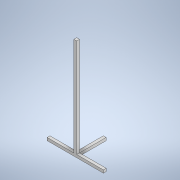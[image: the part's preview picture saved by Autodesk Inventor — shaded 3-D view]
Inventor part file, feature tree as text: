
AUTODESK INVENTOR PART (.ipt)
format: ipt  version: 2020 (Build 240168000, 168)  size: 119,808 bytes
history: native  units: mm
features: extrude x3, sketch x3, projected_geometry x1
ambient origin geometry x8: Origin, YZ Plane, XZ Plane, XY Plane, X Axis, Y Axis, Z Axis, Center Point
bodies: Solid1 (feature_tree)
feature tree (7):
  extrude  "Extrusion1"  Depth=20.0mm
  extrude  "Extrusion2"  Depth=400.0mm
  extrude  "Extrusion3"  Depth=20.0mm TaperAngle=0.0deg
  sketch  "Sketch1"  dims[d0=20.0mm d1=20.0mm]
  sketch  "Sketch2"  dims[d2=700.0mm d3=0.0mm d4=400.0mm]
  sketch  "Sketch3"  dims[d5=20.0mm d6=20.0mm d7=0.0mm d8=200.0mm d9=20.0mm d10=200.0mm d11=20.0mm d12=0.0mm]
  projected_geometry  "Projected Loop1"
